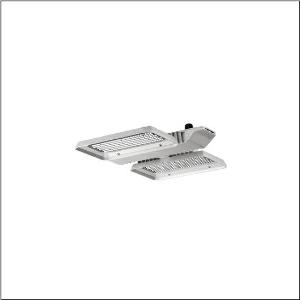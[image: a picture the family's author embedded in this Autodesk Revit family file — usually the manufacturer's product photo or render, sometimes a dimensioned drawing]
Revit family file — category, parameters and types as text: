
# Revit family: highbay_11_51hla2d14fcad
name_source: partatom
category: Lighting Fixtures
units: mm (PartAtom-declared; Revit-internal decimal feet)

## family parameters
Cut with Voids When Loaded = No
Host = Face
Light Source = No
Part Type = Normal
Room Calculation Point = No
Round Connector Dimension = Use Diameter
Shared = No

## types (1)
- --- (1 x LED, 2160 lm, 14 W, 4000K)
    Apparent Load = 14 VA
    CIE Flux Codes = 89 96 99 100 100
    Color Rendering = 80
    Color Temperature = 4000K
    Default Elevation = 1800 mm
    Description = Highbay 11, LED high bay luminaire, primary light control with lens, of PMMA, light emission: direct distribution, primary light characteristic: symmetric, installation type: suspended mounting, surface-mounted, for 1x 2x LED, rated luminous flux: 14.400lm, luminous efficacy: 177lm/W, light colour: 840, colour temperature: 4000K, control gear: ECG DALI, with terminal, 5-pole, max. 2.5mm², mains connection: 230..240V, AC/DC, 50/60Hz, rated input power: 81W, LED unit, of diecast aluminium, bead blasted, unplated, silver, length: 470mm, width: 500mm, height: 65mm, housing, of diecast aluminium, bead blasted, uncoated, silver, protection rating (complete): IP65, insulation class (complete): insulation class I (protective earthing), certification: CE, UKCA, protection symbol: D, impact resistance: IK08 with glass or PC cover, permissible operating ambient temperature: -35..+55°C, standard: EN 60598-2-22, reducing of maximum allowable ambient temperature of 5°C with ceiling mounting, corresponds to IFS (International Featured Standards) requirements for safety and quality in the food industry, packaging unit: 1 piece
    Height = 95 mm
    Lamp = 1 x LED
    Lamp Light Flux = 2160 lm
    Lamp Power = 14 W
    Lamp count = 1
    Length = 468 mm
    Luminous efficacy = 154 lm/W
    Manufacturer = Siteco
    ModVariant = No
    Model = 51HLA2D14FCAD
    Mounting Place = Ceiling
    Mounting Type = Pendant
    Number of Poles = 1
    OnlyDefault = Yes
    Power Factor = 1
    Product Name = Highbay 11
    Product group = LED high bay luminaire
    ProductGroupID = 903
    Protection Class = Protection class I
    Protection Degree = IP 65
    RLX_Detail_Level = 1
    RLX_Emergency_Light_Flux = 0 lm
    RLX_Emergency_Type = 0
    RLX_Emergency_Type_DB = No
    RlxData = <blob elided: 86737 chars, md5=4d9a6bcb>
    Socket = socket
    Standby Power = 0 W
    System Light Flux = 2160 lm
    System Power = 14 W
    Type Comments = : central accumulator DC – ECG emengency level 15%
    Type Image = l_1003425.jpg
    URL = http://relux.com
    VarID = @adj_171753
    Voltage = 0 V
    Weight = 0.00 kg
    Width = 501 mm

## geometry (parser evidence)
native form markers: Blend x4, Sweep x12
no freeform markers — native parametric forms only
